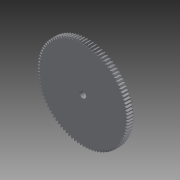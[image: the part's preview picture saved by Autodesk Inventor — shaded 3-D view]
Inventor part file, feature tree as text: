
AUTODESK INVENTOR PART (.ipt)
format: ipt  version: 2013 SP2 (Build 170200200, 200)  size: 907,264 bytes
history: native  units: in
note: dims shown in document units (in); Inventor stores cm internally (conversion verified against a paired STEP export)
features: imported_body x1, extrude x1, sketch x1
ambient origin geometry x8: Origin, YZ Plane, XZ Plane, XY Plane, X Axis, Y Axis, Z Axis, Center Point
bodies: Solid1 (feature_tree)
feature tree (3):
  imported_body  "Base1"
  extrude  "Extrusion4"  [1 undecoded]
  sketch  "Sketch4"  dims[d14=0.3in d15=0.0in]
note: 1 required parameter value undecoded (feature->parameter linkage not recoverable at this tier; creation-order binding heuristic only, values carry confidence <= 0.55)
